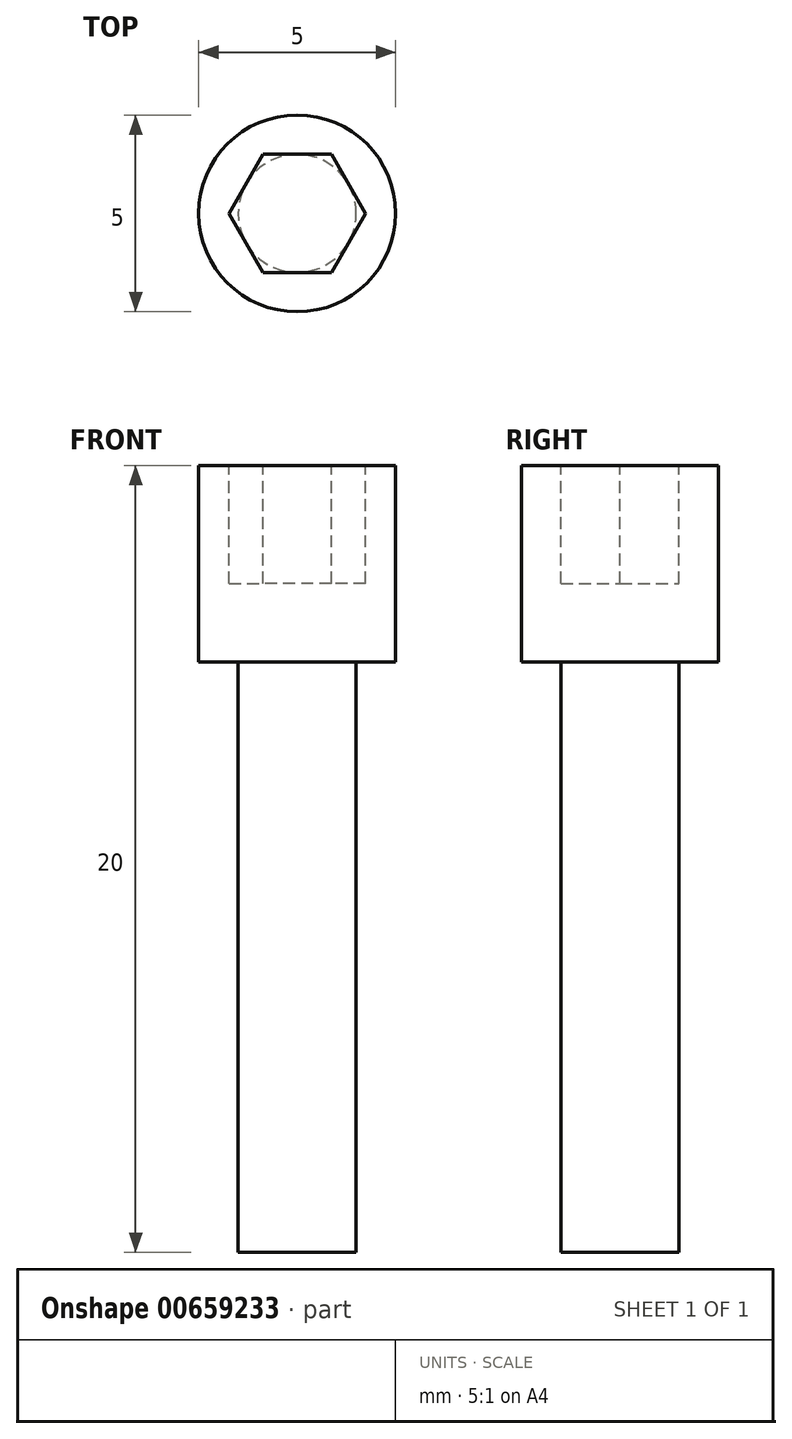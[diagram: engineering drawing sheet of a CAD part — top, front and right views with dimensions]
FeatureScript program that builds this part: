
annotation { "Feature Type Name" : "Feature", "Feature Type Description" : "" }
export const myFeature = defineFeature(function(context is Context, id is Id, definition is map)
    precondition{}
    {
        {
            var Q0;
            Q0=qCreatedBy(makeId("Top.planeOp"),FACE);
            var sketch = newSketch(context, id + "F0", { "sketchPlane" : qUnion([Q0])});
            skCircle(sketch, "E0", {"center": v(0, 0) * mm, "radius": 1.5 * mm});
            skSolve(sketch);
        }
        {
            var Q0;
            Q0=makeQuery(id+"F0.imprint","IMPRINT",FACE,{"disambiguationData":[TD([[makeQuery(id+"F0.imprint","IMPRINT",EDGE,{"derivedFrom":sQuery(id+"F0.wireOp",EDGE,"E0")}),1.0]])]});
            extrude(context, id + "F1", {"entities" : qUnion([Q0]), "oppositeDirection" : true, "depth" : 15 * mm, "offsetDistance" : 25 * mm});
        }
        {
            var Q0;
            Q0=makeQuery(id+"F1.opExtrude","CAP_FACE",FACE,{"disambiguationData":[OSD([sQuery(id+"F0.wireOp",EDGE,"E0")])],"isStart":true});
            var sketch = newSketch(context, id + "F2", { "sketchPlane" : qUnion([Q0])});
            skCircle(sketch, "E1", {"center": v(0, 0) * mm, "radius": 2.5 * mm});
            skSolve(sketch);
        }
        {
            var Q0;
            Q0=makeQuery(id+"F2.imprint","IMPRINT",FACE,{"disambiguationData":[TD([[makeQuery(id+"F2.imprint","IMPRINT",EDGE,{"derivedFrom":sQuery(id+"F2.wireOp",EDGE,"E1")}),1.0]])]});
            var Q1;
            Q1=makeQuery(id+"F2.imprint","IMPRINT",FACE,{"disambiguationData":[TD([[makeQuery(id+"F2.imprint","IMPRINT",EDGE,{"derivedFrom":makeQuery(id+"F1.opExtrude","CAP_EDGE",EDGE,{"disambiguationData":[OSD([sQuery(id+"F0.wireOp",EDGE,"E0")])],"isStart":true})}),1.0]])]});
            extrude(context, id + "F3", {"entities" : qUnion([Q0, Q1]), "operationType" : NewBodyOperationType.ADD, "depth" : 5 * mm, "offsetDistance" : 25 * mm});
        }
        {
            var Q0;
            Q0=makeQuery(id+"F3.opExtrude","CAP_FACE",FACE,{"disambiguationData":[OSD([sQuery(id+"F2.wireOp",EDGE,"E1")])],"isStart":false});
            var sketch = newSketch(context, id + "F4", { "sketchPlane" : qUnion([Q0])});
            skCircle(sketch, "E2.cCircle", {"center": v(0, 0) * mm, "radius": 1.73 * mm, "construction": true});
            skLineSegment(sketch, "E2.0", {"start": v(-1.73, 0) * mm, "end": v(-0.87, 1.5) * mm});
            skLineSegment(sketch, "E2.1", {"start": v(-0.87, 1.5) * mm, "end": v(0.87, 1.5) * mm});
            skLineSegment(sketch, "E2.2", {"start": v(0.87, 1.5) * mm, "end": v(1.73, 0) * mm});
            skLineSegment(sketch, "E2.3", {"start": v(1.73, 0) * mm, "end": v(0.87, -1.5) * mm});
            skLineSegment(sketch, "E2.4", {"start": v(0.87, -1.5) * mm, "end": v(-0.87, -1.5) * mm});
            skLineSegment(sketch, "E2.5", {"start": v(-0.87, -1.5) * mm, "end": v(-1.73, 0) * mm});
            skSolve(sketch);
        }
        {
            var Q0;
            Q0=makeQuery(id+"F4.imprint","IMPRINT",FACE,{"disambiguationData":[TD([[makeQuery(id+"F4.imprint","IMPRINT",EDGE,{"derivedFrom":sQuery(id+"F4.wireOp",EDGE,"E2.0")}),-1.0]])]});
            extrude(context, id + "F5", {"entities" : qUnion([Q0]), "operationType" : NewBodyOperationType.REMOVE, "oppositeDirection" : true, "depth" : 3 * mm, "offsetDistance" : 25 * mm});
        }
    });
